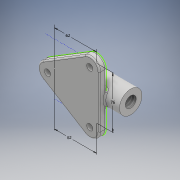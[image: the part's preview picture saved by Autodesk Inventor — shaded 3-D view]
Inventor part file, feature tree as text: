
AUTODESK INVENTOR PART (.ipt)
format: ipt  version: 2018 (Build 220112000, 112)  size: 233,984 bytes
history: native  units: mm
features: sketch x5, extrude x5, thread x1, fillet x1
ambient origin geometry x8: Origin, YZ Plane, XZ Plane, XY Plane, X Axis, Y Axis, Z Axis, Center Point
bodies: Solid1 (feature_tree)
feature tree (12):
  sketch  "Sketch1"  dims[d8=10.0mm d9=0.0mm d10=9.0mm]
  extrude  "Extrusion1"  Depth=10.0mm
  extrude  "Extrusion2"  Depth=10.0mm
  extrude  "Extrusion6"  Depth=62.0mm
  extrude  "Extrusion7"  Depth=9.0mm
  extrude  "Extrusion8"  Depth=2.0mm
  thread  "Thread2"  [1 undecoded]
  fillet  "Fillet11"  Radius=48.0mm
  sketch  "Sketch2"  dims[d15=10.0mm d16=0.0mm d37=62.0mm]
  sketch  "Sketch9"  dims[d40=76.0mm d41=62.0mm]
  sketch  "Sketch10"  dims[d42=9.0mm d43=9.0mm]
  sketch  "Sketch11"  dims[d44=62.0mm d46=24.0mm d47=33.0mm d48=48.0mm d49=0.0mm d50=22.0mm d51=0.0mm d52=16.0mm d53=70.0mm d54=0.0mm d55=10.0mm d56=0.0mm d63=2.0mm d29=1.0mm d30=1.0mm]
note: 1 required parameter value undecoded (feature->parameter linkage not recoverable at this tier; creation-order binding heuristic only, values carry confidence <= 0.55)
